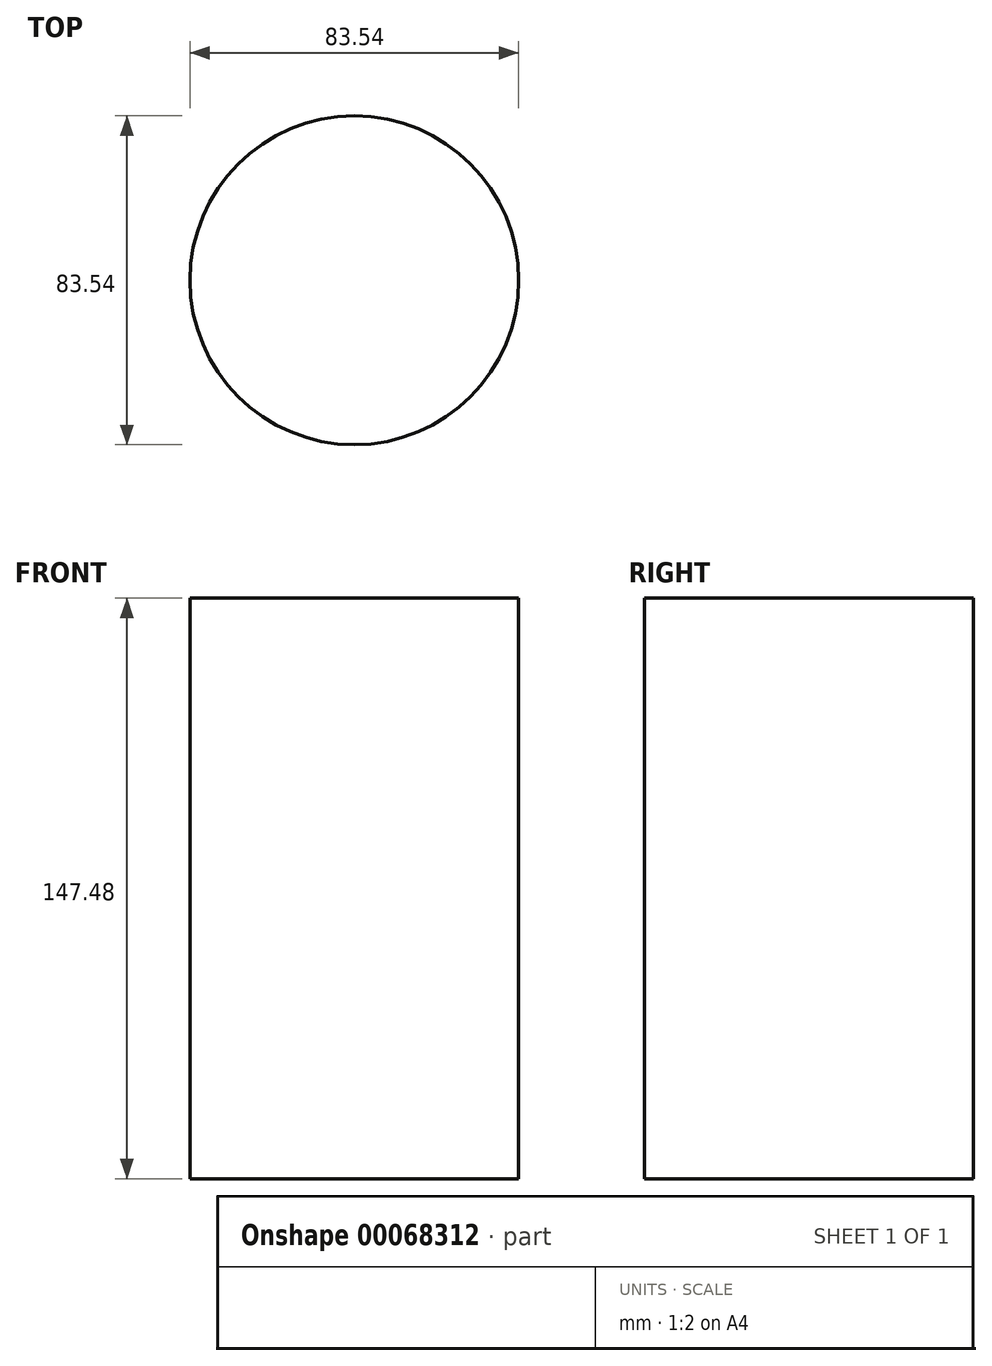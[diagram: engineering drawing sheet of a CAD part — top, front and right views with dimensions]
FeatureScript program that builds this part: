
annotation { "Feature Type Name" : "Feature", "Feature Type Description" : "" }
export const myFeature = defineFeature(function(context is Context, id is Id, definition is map)
    precondition{}
    {
        {
            var Q0;
            Q0=qCreatedBy(makeId("Top.planeOp"),FACE);
            var sketch = newSketch(context, id + "F0", { "sketchPlane" : qUnion([Q0])});
            skCircle(sketch, "E0", {"center": v(0, 0) * mm, "radius": 41.77 * mm});
            skSolve(sketch);
        }
        {
            var Q0;
            Q0=makeQuery(id+"F0.imprint","IMPRINT",FACE,{"disambiguationData":[TD([[makeQuery(id+"F0.imprint","IMPRINT",EDGE,{"derivedFrom":sQuery(id+"F0.wireOp",EDGE,"E0")}),1.0]])]});
            extrude(context, id + "F1", {"entities" : qUnion([Q0]), "depth" : 147.48 * mm});
        }
    });
